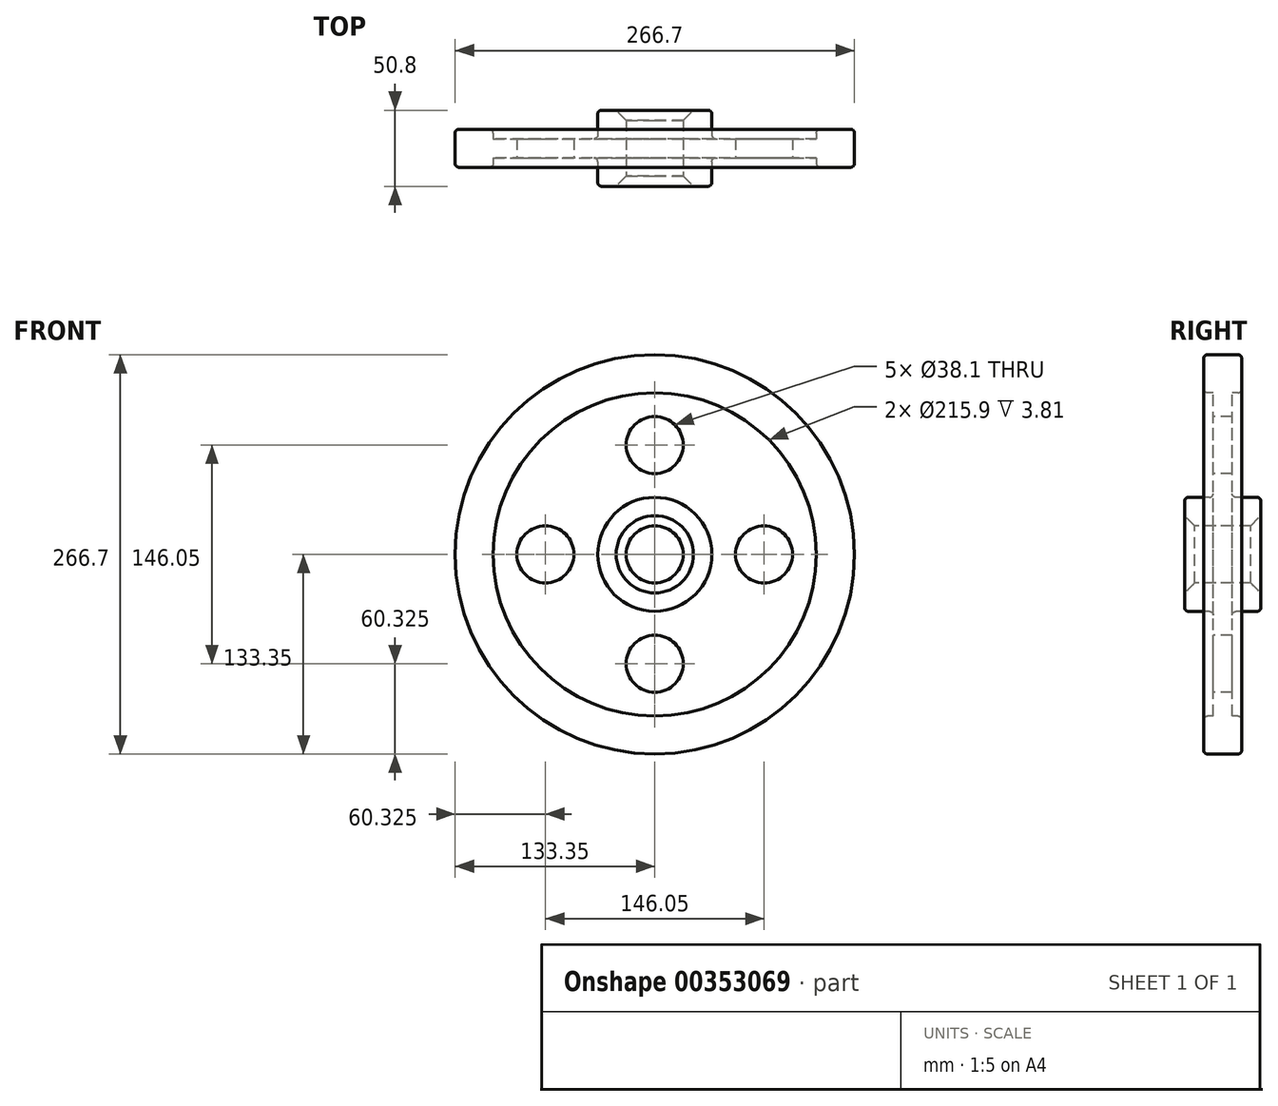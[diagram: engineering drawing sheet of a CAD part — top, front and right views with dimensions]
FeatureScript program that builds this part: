
annotation { "Feature Type Name" : "Feature", "Feature Type Description" : "" }
export const myFeature = defineFeature(function(context is Context, id is Id, definition is map)
    precondition{}
    {
        {
            var Q0;
            Q0=qCreatedBy(makeId("Right.planeOp"),FACE);
            var sketch = newSketch(context, id + "F0", { "sketchPlane" : qUnion([Q0])});
            skLineSegment(sketch, "E0", {"start": v(0, 0) * mm, "end": v(25.4, 0) * mm, "construction": true});
            skLineSegment(sketch, "E1.0", {"start": v(0, 19.05) * mm, "end": v(25.4, 19.05) * mm});
            skLineSegment(sketch, "E2.0", {"start": v(0, 38.1) * mm, "end": v(25.4, 38.1) * mm});
            skLineSegment(sketch, "E3.0", {"start": v(6.35, 107.95) * mm, "end": v(12.7, 107.95) * mm});
            skLineSegment(sketch, "E4.0", {"start": v(0, 133.35) * mm, "end": v(12.7, 133.35) * mm});
            skLineSegment(sketch, "E5", {"start": v(0, 0) * mm, "end": v(0, 133.35) * mm});
            skLineSegment(sketch, "E6.0", {"start": v(25.4, 19.05) * mm, "end": v(25.4, 38.1) * mm});
            skLineSegment(sketch, "E7.1", {"start": v(6.35, 38.1) * mm, "end": v(6.35, 107.95) * mm});
            skLineSegment(sketch, "E8.trimOffspring", {"start": v(24, 73.03) * mm, "end": v(25.4, 73.03) * mm});
            skLineSegment(sketch, "E9.trimOffspring", {"start": v(12.7, 107.95) * mm, "end": v(12.7, 133.35) * mm});
            skLineSegment(sketch, "E10.MirrorCS", {"start": v(-25.4, 19.05) * mm, "end": v(-25.4, 38.1) * mm});
            skLineSegment(sketch, "E11.MirrorCS", {"start": v(0, 19.05) * mm, "end": v(-25.4, 19.05) * mm});
            skLineSegment(sketch, "E12.MirrorCS", {"start": v(0, 38.1) * mm, "end": v(-25.4, 38.1) * mm});
            skLineSegment(sketch, "E13.MirrorCS", {"start": v(-6.35, 38.1) * mm, "end": v(-6.35, 107.95) * mm});
            skLineSegment(sketch, "E14.MirrorCS", {"start": v(-12.7, 107.95) * mm, "end": v(-12.7, 133.35) * mm});
            skLineSegment(sketch, "E15.MirrorCS", {"start": v(0, 133.35) * mm, "end": v(-12.7, 133.35) * mm});
            skLineSegment(sketch, "E16.MirrorCS", {"start": v(-6.35, 107.95) * mm, "end": v(-12.7, 107.95) * mm});
            skLineSegment(sketch, "E17", {"start": v(0, 0) * mm, "end": v(76.06, 0) * mm, "construction": true});
            skSolve(sketch);
        }
        {
            var Q0;
            Q0=makeQuery(id+"F0.imprint","IMPRINT",FACE,{"disambiguationData":[TD([[makeQuery(id+"F0.imprint","IMPRINT",EDGE,{"derivedFrom":sQuery(id+"F0.wireOp",EDGE,"E3.0")}),1.0]])]});
            var Q1;
            {var subQ0=sQuery(id+"F0.wireOp",EDGE,"E13.MirrorCS");Q1=makeQuery(id+"F0.imprint","IMPRINT",FACE,{"disambiguationData":[TD([[makeQuery(id+"F0.imprint","IMPRINT",EDGE,{"derivedFrom":subQ0}),-1.0]])]});}
            var Q2;
            {var subQ5=sQuery(id+"F0.wireOp",EDGE,"E1.0");Q2=makeQuery(id+"F0.imprint","IMPRINT",FACE,{"disambiguationData":[TD([[makeQuery(id+"F0.imprint","IMPRINT",EDGE,{"derivedFrom":subQ5}),1.0]])]});}
            var Q3;
            {var subQ5=sQuery(id+"F0.wireOp",EDGE,"E10.MirrorCS");Q3=makeQuery(id+"F0.imprint","IMPRINT",FACE,{"disambiguationData":[TD([[makeQuery(id+"F0.imprint","IMPRINT",EDGE,{"derivedFrom":subQ5}),-1.0]])]});}
            var Q4;
            Q4=sQuery(id+"F0.wireOp",EDGE,"E17");
            revolve(context, id + "F1", {"entities" : qUnion([Q0, Q1, Q2, Q3]), "axis" : qUnion([Q4]), "revolveType" : RevolveType.FULL});
        }
        {
            var Q0;
            Q0=makeQuery(id+"F1.opRevolve","SWEPT_FACE",FACE,{"disambiguationData":[OSD([sQuery(id+"F0.wireOp",EDGE,"E13.MirrorCS")])]});
            var sketch = newSketch(context, id + "F2", { "sketchPlane" : qUnion([Q0])});
            skLineSegment(sketch, "E18", {"start": v(0, 0) * mm, "end": v(0, 73.03) * mm});
            skCircle(sketch, "E19", {"center": v(0, 73.03) * mm, "radius": 19.05 * mm});
            skCircle(sketch, "E20.1.0", {"center": v(-73.03, 0) * mm, "radius": 19.05 * mm});
            skCircle(sketch, "E20.2.0", {"center": v(0, -73.03) * mm, "radius": 19.05 * mm});
            skCircle(sketch, "E20.3.0", {"center": v(73.03, 0) * mm, "radius": 19.05 * mm});
            skPoint(sketch, "E20.center", {"position": v(0, 0) * mm});
            skSolve(sketch);
        }
        {
            var Q0;
            Q0=makeQuery(id+"F2.imprint","IMPRINT",FACE,{"disambiguationData":[TD([[makeQuery(id+"F2.imprint","IMPRINT",EDGE,{"derivedFrom":sQuery(id+"F2.wireOp",EDGE,"E20.1.0")}),1.0]])]});
            var Q1;
            Q1=makeQuery(id+"F2.imprint","IMPRINT",FACE,{"disambiguationData":[TD([[makeQuery(id+"F2.imprint","IMPRINT",EDGE,{"derivedFrom":sQuery(id+"F2.wireOp",EDGE,"E20.2.0")}),1.0]])]});
            var Q2;
            Q2=makeQuery(id+"F2.imprint","IMPRINT",FACE,{"disambiguationData":[TD([[makeQuery(id+"F2.imprint","IMPRINT",EDGE,{"derivedFrom":sQuery(id+"F2.wireOp",EDGE,"E20.3.0")}),1.0]])]});
            var Q3;
            Q3=makeQuery(id+"F2.imprint","IMPRINT",FACE,{"disambiguationData":[TD([[makeQuery(id+"F2.imprint","IMPRINT",EDGE,{"derivedFrom":sQuery(id+"F2.wireOp",EDGE,"E19")}),1.0]])]});
            extrude(context, id + "F3", {"entities" : qUnion([Q0, Q1, Q2, Q3]), "operationType" : NewBodyOperationType.REMOVE, "oppositeDirection" : true, "depth" : 25.4 * mm});
        }
        {
            var Q0;
            Q0=makeQuery(id+"F1.opRevolve","SWEPT_EDGE",EDGE,{"disambiguationData":[OSD([sQuery(id+"F0.wireOp",EDGE,"E12.MirrorCS"),sQuery(id+"F0.wireOp",EDGE,"E13.MirrorCS")])]});
            var Q1;
            Q1=makeQuery(id+"F1.opRevolve","SWEPT_EDGE",EDGE,{"disambiguationData":[OSD([sQuery(id+"F0.wireOp",EDGE,"E10.MirrorCS"),sQuery(id+"F0.wireOp",EDGE,"E12.MirrorCS")])]});
            var Q2;
            Q2=makeQuery(id+"F1.opRevolve","SWEPT_EDGE",EDGE,{"disambiguationData":[OSD([sQuery(id+"F0.wireOp",EDGE,"E14.MirrorCS"),sQuery(id+"F0.wireOp",EDGE,"E16.MirrorCS")])]});
            var Q3;
            Q3=makeQuery(id+"F1.opRevolve","SWEPT_EDGE",EDGE,{"disambiguationData":[OSD([sQuery(id+"F0.wireOp",EDGE,"E14.MirrorCS"),sQuery(id+"F0.wireOp",EDGE,"E15.MirrorCS")])]});
            var Q4;
            Q4=makeQuery(id+"F1.opRevolve","SWEPT_EDGE",EDGE,{"disambiguationData":[OSD([sQuery(id+"F0.wireOp",EDGE,"E2.0"),sQuery(id+"F0.wireOp",EDGE,"E6.0")])]});
            fillet(context, id + "F4", {"entities" : qUnion([Q0, Q1, Q2, Q3, Q4]), "radius" : 2.54 * mm, "tangentPropagation" : true, "allowEdgeOverflow" : false});
        }
        {
            var Q0;
            {var subQ0=sQuery(id+"F0.wireOp",EDGE,"E6.0");Q0=makeQuery(id+"F4.opFillet","BLEND_EDGE",EDGE,{"blendedFrom":[makeQuery(id+"F1.opRevolve","SWEPT_EDGE",EDGE,{"disambiguationData":[OSD([sQuery(id+"F0.wireOp",EDGE,"E2.0"),subQ0])]}),makeQuery(id+"F1.opRevolve","SWEPT_FACE",FACE,{"disambiguationData":[OSD([subQ0])]})],"blendedInto":[makeQuery(id+"F1.opRevolve","SWEPT_FACE",FACE,{"disambiguationData":[OSD([subQ0])]})]});}
            var Q1;
            Q1=makeQuery(id+"F1.opRevolve","SWEPT_EDGE",EDGE,{"disambiguationData":[OSD([sQuery(id+"F0.wireOp",EDGE,"E2.0"),sQuery(id+"F0.wireOp",EDGE,"E7.1")])]});
            var Q2;
            Q2=makeQuery(id+"F1.opRevolve","SWEPT_EDGE",EDGE,{"disambiguationData":[OSD([sQuery(id+"F0.wireOp",EDGE,"E3.0"),sQuery(id+"F0.wireOp",EDGE,"E9.trimOffspring")])]});
            var Q3;
            Q3=makeQuery(id+"F1.opRevolve","SWEPT_EDGE",EDGE,{"disambiguationData":[OSD([sQuery(id+"F0.wireOp",EDGE,"E4.0"),sQuery(id+"F0.wireOp",EDGE,"E9.trimOffspring")])]});
            fillet(context, id + "F5", {"entities" : qUnion([Q0, Q1, Q2, Q3]), "radius" : 2.54 * mm, "tangentPropagation" : true, "allowEdgeOverflow" : false});
        }
        {
            var Q0;
            Q0=makeQuery(id+"F1.opRevolve","SWEPT_EDGE",EDGE,{"disambiguationData":[OSD([sQuery(id+"F0.wireOp",EDGE,"E10.MirrorCS"),sQuery(id+"F0.wireOp",EDGE,"E11.MirrorCS")])]});
            var Q1;
            Q1=makeQuery(id+"F1.opRevolve","SWEPT_EDGE",EDGE,{"disambiguationData":[OSD([sQuery(id+"F0.wireOp",EDGE,"E1.0"),sQuery(id+"F0.wireOp",EDGE,"E6.0")])]});
            chamfer(context, id + "F6", {"entities" : qUnion([Q0, Q1]), "width" : 6.73 * mm, "tangentPropagation" : true});
        }
    });
